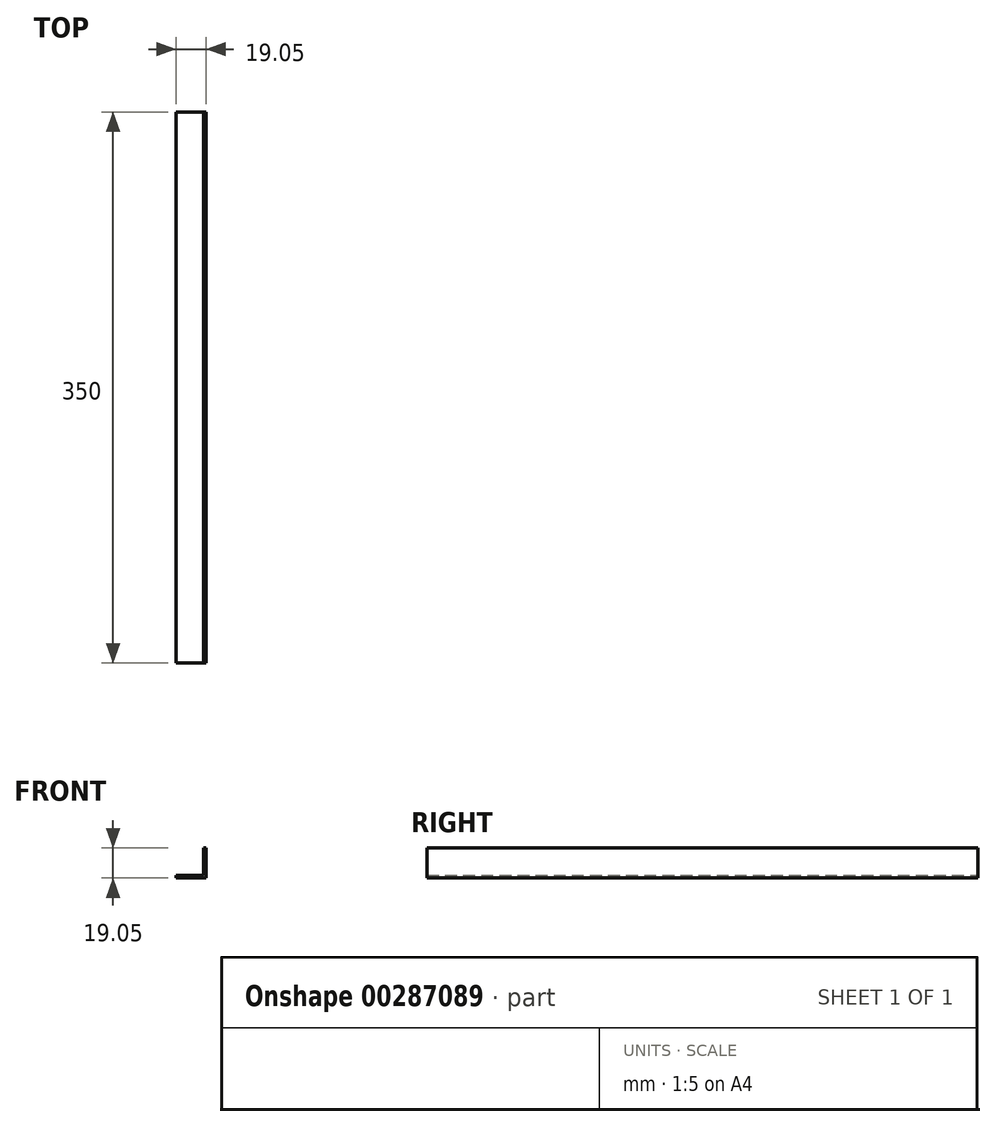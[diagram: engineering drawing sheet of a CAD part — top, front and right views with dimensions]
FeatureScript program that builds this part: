
annotation { "Feature Type Name" : "Feature", "Feature Type Description" : "" }
export const myFeature = defineFeature(function(context is Context, id is Id, definition is map)
    precondition{}
    {
        {
            var Q0;
            Q0=qCreatedBy(makeId("Front.planeOp"),FACE);
            var sketch = newSketch(context, id + "F0", { "sketchPlane" : qUnion([Q0])});
            skLineSegment(sketch, "E0", {"start": v(-19.05, 0) * mm, "end": v(0, 0) * mm});
            skLineSegment(sketch, "E1", {"start": v(0, 0) * mm, "end": v(0, 19.05) * mm});
            skLineSegment(sketch, "E2.0", {"start": v(-1.59, 1.59) * mm, "end": v(-1.59, 19.05) * mm});
            skLineSegment(sketch, "E2.1", {"start": v(-19.05, 1.59) * mm, "end": v(-1.59, 1.59) * mm});
            skLineSegment(sketch, "E3", {"start": v(0, 19.05) * mm, "end": v(-1.59, 19.05) * mm});
            skLineSegment(sketch, "E4", {"start": v(-19.05, 1.59) * mm, "end": v(-19.05, 0) * mm});
            skSolve(sketch);
        }
        {
            var Q0;
            Q0=qSketchRegion(id+"F0",true);
            extrude(context, id + "F1", {"entities" : qUnion([Q0]), "depth" : 350 * mm});
        }
    });
